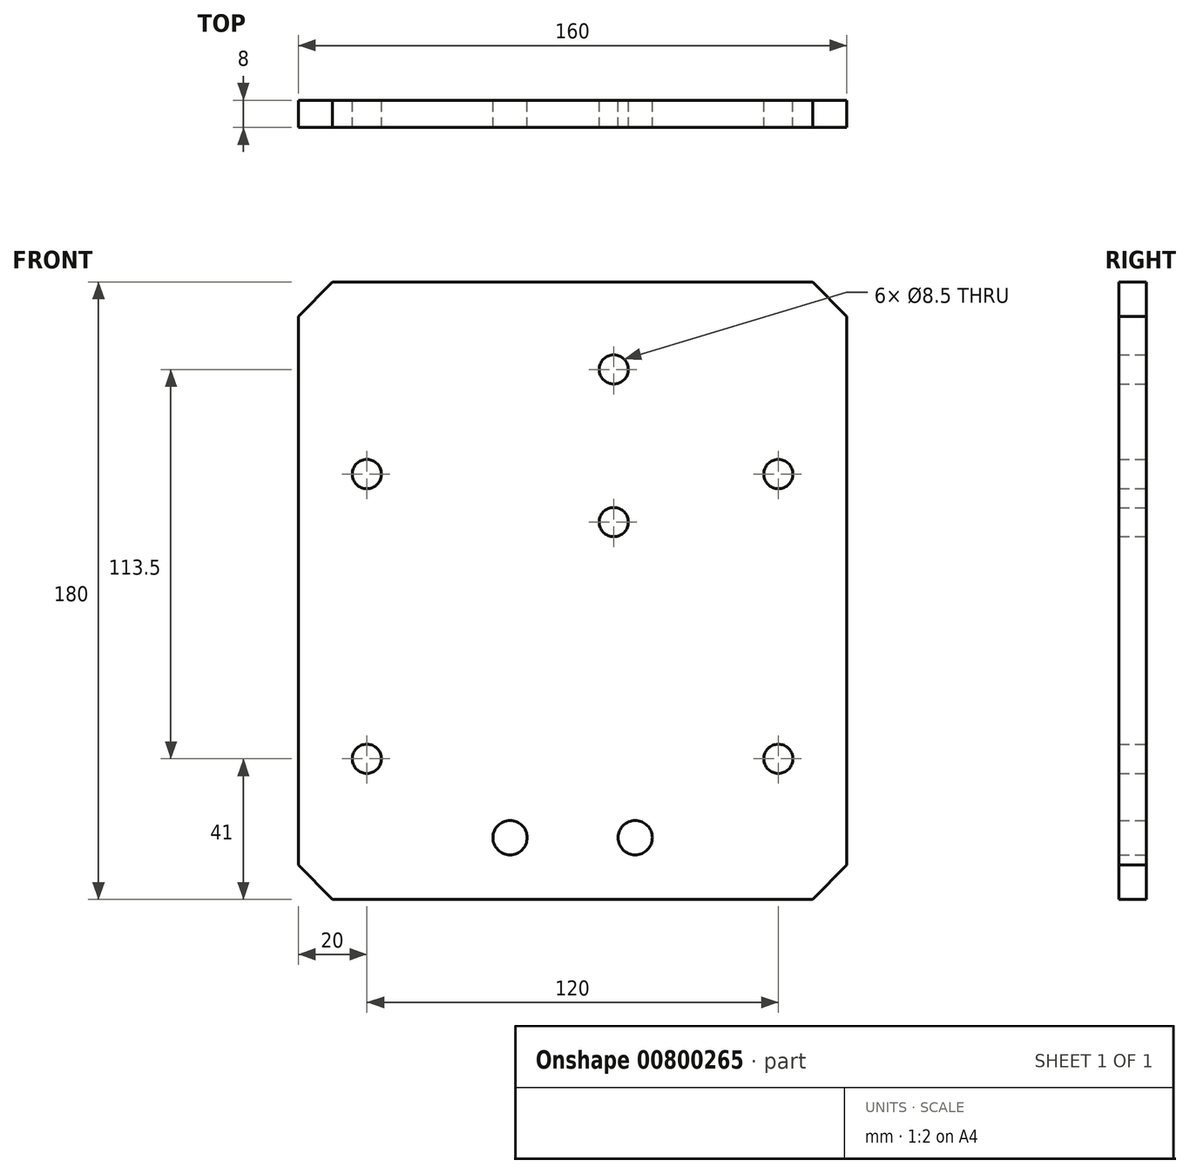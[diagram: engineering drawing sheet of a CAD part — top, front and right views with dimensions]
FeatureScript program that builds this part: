
annotation { "Feature Type Name" : "Feature", "Feature Type Description" : "" }
export const myFeature = defineFeature(function(context is Context, id is Id, definition is map)
    precondition{}
    {
        {
            var Q0;
            Q0=qCreatedBy(makeId("Front.planeOp"),FACE);
            var sketch = newSketch(context, id + "F0", { "sketchPlane" : qUnion([Q0])});
            skLineSegment(sketch, "E0.bottom", {"start": v(-80, 90) * mm, "end": v(80, 90) * mm});
            skLineSegment(sketch, "E0.top", {"start": v(-80, -90) * mm, "end": v(80, -90) * mm});
            skLineSegment(sketch, "E0.left", {"start": v(-80, 90) * mm, "end": v(-80, -90) * mm});
            skLineSegment(sketch, "E0.right", {"start": v(80, 90) * mm, "end": v(80, -90) * mm});
            skLineSegment(sketch, "E1", {"start": v(0, 90) * mm, "end": v(0, -90) * mm, "construction": true});
            skLineSegment(sketch, "E2", {"start": v(-80, 0) * mm, "end": v(80, 0) * mm, "construction": true});
            skCircle(sketch, "E3", {"center": v(-18.25, -72) * mm, "radius": 5 * mm});
            skCircle(sketch, "E4", {"center": v(18.25, -72) * mm, "radius": 5 * mm});
            skCircle(sketch, "E5", {"center": v(12, 20) * mm, "radius": 4.25 * mm});
            skCircle(sketch, "E6", {"center": v(12, 64.5) * mm, "radius": 4.25 * mm});
            skCircle(sketch, "E7", {"center": v(60, 34) * mm, "radius": 4.25 * mm});
            skCircle(sketch, "E8", {"center": v(60, -49) * mm, "radius": 4.25 * mm});
            skCircle(sketch, "E9", {"center": v(-60, -49) * mm, "radius": 4.25 * mm});
            skCircle(sketch, "E10", {"center": v(-60, 34) * mm, "radius": 4.25 * mm});
            skLineSegment(sketch, "E11", {"start": v(-60, 34) * mm, "end": v(60, 34) * mm, "construction": true});
            skLineSegment(sketch, "E12", {"start": v(60, -49) * mm, "end": v(60, 34) * mm, "construction": true});
            skLineSegment(sketch, "E13", {"start": v(-60, 34) * mm, "end": v(-60, -49) * mm, "construction": true});
            skLineSegment(sketch, "E14", {"start": v(-60, -49) * mm, "end": v(60, -49) * mm, "construction": true});
            skLineSegment(sketch, "E15", {"start": v(-18.25, -72) * mm, "end": v(18.25, -72) * mm, "construction": true});
            skLineSegment(sketch, "E16", {"start": v(12, 20) * mm, "end": v(12, 64.5) * mm, "construction": true});
            skSolve(sketch);
        }
        {
            var Q0;
            Q0 = qSketchRegion(id + "F0", true);
            extrude(context, id + "F1", {"entities" : qUnion([Q0]), "depth" : 8 * mm, "offsetDistance" : 25 * mm});
        }
        {
            var Q0;
            Q0=makeQuery(id+"F1.opExtrude","SWEPT_EDGE",EDGE,{"disambiguationData":[OSD([sQuery(id+"F0.wireOp",EDGE,"E0.bottom"),sQuery(id+"F0.wireOp",EDGE,"E0.left")])]});
            var Q1;
            Q1=makeQuery(id+"F1.opExtrude","SWEPT_EDGE",EDGE,{"disambiguationData":[OSD([sQuery(id+"F0.wireOp",EDGE,"E0.bottom"),sQuery(id+"F0.wireOp",EDGE,"E0.right")])]});
            var Q2;
            Q2=makeQuery(id+"F1.opExtrude","SWEPT_EDGE",EDGE,{"disambiguationData":[OSD([sQuery(id+"F0.wireOp",EDGE,"E0.top"),sQuery(id+"F0.wireOp",EDGE,"E0.right")])]});
            var Q3;
            Q3=makeQuery(id+"F1.opExtrude","SWEPT_EDGE",EDGE,{"disambiguationData":[OSD([sQuery(id+"F0.wireOp",EDGE,"E0.top"),sQuery(id+"F0.wireOp",EDGE,"E0.left")])]});
            chamfer(context, id + "F2", {"entities" : qUnion([Q0, Q1, Q2, Q3]), "width" : 10 * mm, "tangentPropagation" : true});
        }
    });
